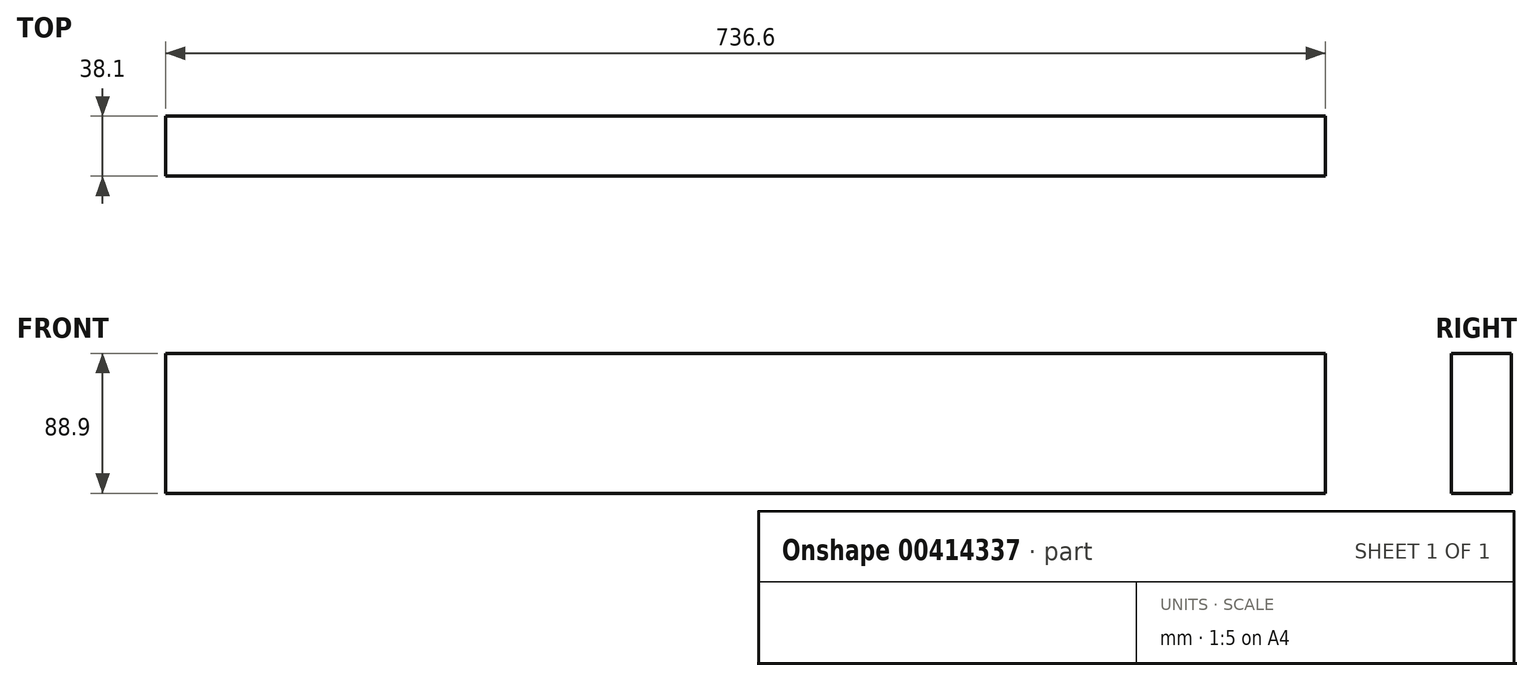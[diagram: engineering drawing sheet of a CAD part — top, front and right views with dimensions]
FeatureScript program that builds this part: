
annotation { "Feature Type Name" : "Feature", "Feature Type Description" : "" }
export const myFeature = defineFeature(function(context is Context, id is Id, definition is map)
    precondition{}
    {
        {
            var Q0;
            Q0=qCreatedBy(makeId("Top.planeOp"),FACE);
            var sketch = newSketch(context, id + "F0", { "sketchPlane" : qUnion([Q0])});
            skLineSegment(sketch, "E0.bottom", {"start": v(368.3, 19.05) * mm, "end": v(-368.3, 19.05) * mm});
            skLineSegment(sketch, "E0.top", {"start": v(368.3, -19.05) * mm, "end": v(-368.3, -19.05) * mm});
            skLineSegment(sketch, "E0.left", {"start": v(368.3, 19.05) * mm, "end": v(368.3, -19.05) * mm});
            skLineSegment(sketch, "E0.right", {"start": v(-368.3, 19.05) * mm, "end": v(-368.3, -19.05) * mm});
            skPoint(sketch, "E0.middle", {"position": v(0, 0) * mm});
            skSolve(sketch);
        }
        {
            var Q0;
            Q0 = qSketchRegion(id + "F0", true);
            extrude(context, id + "F1", {"entities" : qUnion([Q0]), "depth" : 88.9 * mm});
        }
    });
